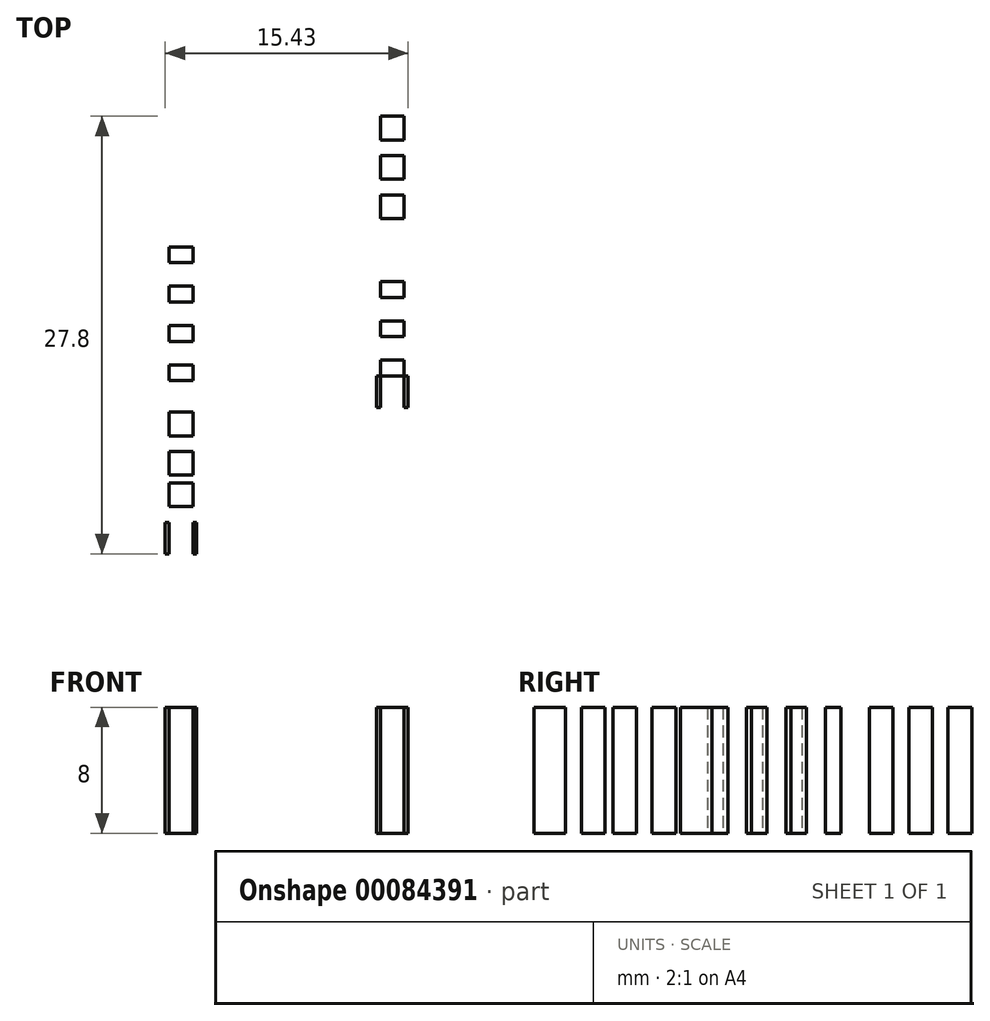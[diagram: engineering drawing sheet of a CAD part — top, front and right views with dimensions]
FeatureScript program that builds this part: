
annotation { "Feature Type Name" : "Feature", "Feature Type Description" : "" }
export const myFeature = defineFeature(function(context is Context, id is Id, definition is map)
    precondition{}
    {
        {
            var Q0;
            Q0=qCreatedBy(makeId("Top.planeOp"),FACE);
            var sketch = newSketch(context, id + "F0", { "sketchPlane" : qUnion([Q0])});
            skLineSegment(sketch, "E0.bottom", {"start": v(-61.05, 1.87) * mm, "end": v(-59.05, 1.87) * mm});
            skLineSegment(sketch, "E0.top", {"start": v(-61.05, -19.13) * mm, "end": v(-59.05, -19.13) * mm});
            skLineSegment(sketch, "E0.left", {"start": v(-61.05, 1.87) * mm, "end": v(-61.05, -19.13) * mm});
            skLineSegment(sketch, "E0.right", {"start": v(-59.05, 1.87) * mm, "end": v(-59.05, -19.13) * mm});
            skLineSegment(sketch, "E1", {"start": v(-61.05, -18.62) * mm, "end": v(-59.05, -18.62) * mm});
            skLineSegment(sketch, "E2", {"start": v(-61.05, -17.12) * mm, "end": v(-59.05, -17.12) * mm});
            skLineSegment(sketch, "E3", {"start": v(-60.8, 1.87) * mm, "end": v(-60.8, -19.13) * mm});
            skLineSegment(sketch, "E4", {"start": v(-60.8, -19.13) * mm, "end": v(-60.05, -19.13) * mm});
            skLineSegment(sketch, "E5", {"start": v(-59.3, 1.87) * mm, "end": v(-59.3, -19.13) * mm});
            skLineSegment(sketch, "E6.bottom", {"start": v(-60.8, 1.87) * mm, "end": v(-59.3, 1.87) * mm});
            skLineSegment(sketch, "E6.top", {"start": v(-60.8, 0.37) * mm, "end": v(-59.3, 0.37) * mm});
            skLineSegment(sketch, "E6.left", {"start": v(-60.8, 1.87) * mm, "end": v(-60.8, 0.37) * mm});
            skLineSegment(sketch, "E6.right", {"start": v(-59.3, 1.87) * mm, "end": v(-59.3, 0.37) * mm});
            skLineSegment(sketch, "E7.top", {"start": v(-60.8, -0.63) * mm, "end": v(-59.3, -0.63) * mm});
            skLineSegment(sketch, "E7.left", {"start": v(-60.8, 0.37) * mm, "end": v(-60.8, -0.63) * mm});
            skLineSegment(sketch, "E7.right", {"start": v(-59.3, 0.37) * mm, "end": v(-59.3, -0.63) * mm});
            skLineSegment(sketch, "E8.top", {"start": v(-60.8, -2.13) * mm, "end": v(-59.3, -2.13) * mm});
            skLineSegment(sketch, "E8.left", {"start": v(-60.8, -0.63) * mm, "end": v(-60.8, -2.13) * mm});
            skLineSegment(sketch, "E8.right", {"start": v(-59.3, -0.63) * mm, "end": v(-59.3, -2.13) * mm});
            skLineSegment(sketch, "E9.top", {"start": v(-60.8, -3.13) * mm, "end": v(-59.3, -3.13) * mm});
            skLineSegment(sketch, "E9.left", {"start": v(-60.8, -2.13) * mm, "end": v(-60.8, -3.13) * mm});
            skLineSegment(sketch, "E9.right", {"start": v(-59.3, -2.13) * mm, "end": v(-59.3, -3.13) * mm});
            skLineSegment(sketch, "E10.top", {"start": v(-60.8, -4.63) * mm, "end": v(-59.3, -4.63) * mm});
            skLineSegment(sketch, "E10.left", {"start": v(-60.8, -3.13) * mm, "end": v(-60.8, -4.63) * mm});
            skLineSegment(sketch, "E10.right", {"start": v(-59.3, -3.13) * mm, "end": v(-59.3, -4.63) * mm});
            skLineSegment(sketch, "E11.left", {"start": v(-60.8, -4.63) * mm, "end": v(-60.8, -5.63) * mm});
            skLineSegment(sketch, "E12.top", {"start": v(-60.8, -10.13) * mm, "end": v(-59.3, -10.13) * mm});
            skLineSegment(sketch, "E12.left", {"start": v(-60.8, -8.63) * mm, "end": v(-60.8, -10.13) * mm});
            skLineSegment(sketch, "E12.right", {"start": v(-59.3, -8.13) * mm, "end": v(-59.3, -10.13) * mm});
            skLineSegment(sketch, "E13.top", {"start": v(-60.8, -11.63) * mm, "end": v(-59.3, -11.63) * mm});
            skLineSegment(sketch, "E13.left", {"start": v(-60.8, -10.13) * mm, "end": v(-60.8, -11.63) * mm});
            skLineSegment(sketch, "E13.right", {"start": v(-59.3, -10.13) * mm, "end": v(-59.3, -11.63) * mm});
            skLineSegment(sketch, "E14.top", {"start": v(-60.8, -12.63) * mm, "end": v(-59.3, -12.63) * mm});
            skLineSegment(sketch, "E14.left", {"start": v(-60.8, -11.63) * mm, "end": v(-60.8, -12.63) * mm});
            skLineSegment(sketch, "E14.right", {"start": v(-59.3, -11.63) * mm, "end": v(-59.3, -12.63) * mm});
            skLineSegment(sketch, "E15.top", {"start": v(-60.8, -14.13) * mm, "end": v(-59.3, -14.13) * mm});
            skLineSegment(sketch, "E15.left", {"start": v(-60.8, -12.63) * mm, "end": v(-60.8, -14.13) * mm});
            skLineSegment(sketch, "E15.right", {"start": v(-59.3, -12.63) * mm, "end": v(-59.3, -14.13) * mm});
            skLineSegment(sketch, "E16.right", {"start": v(-59.3, -4.63) * mm, "end": v(-59.3, -5.63) * mm});
            skLineSegment(sketch, "E17", {"start": v(-60.8, -4.63) * mm, "end": v(-60.8, -6.63) * mm});
            skLineSegment(sketch, "E18", {"start": v(-59.3, -6.63) * mm, "end": v(-59.3, -4.63) * mm});
            skLineSegment(sketch, "E19", {"start": v(-59.3, -5.63) * mm, "end": v(-59.3, -4.63) * mm});
            skLineSegment(sketch, "E20", {"start": v(-60.8, -5.63) * mm, "end": v(-59.3, -5.63) * mm});
            skLineSegment(sketch, "E21", {"start": v(-60.8, -5.63) * mm, "end": v(-60.8, -7.13) * mm});
            skLineSegment(sketch, "E22", {"start": v(-59.3, -6.63) * mm, "end": v(-59.3, -5.63) * mm});
            skLineSegment(sketch, "E23", {"start": v(-60.8, -7.13) * mm, "end": v(-59.3, -7.13) * mm});
            skLineSegment(sketch, "E24.trimOffspring", {"start": v(-60.8, -6.63) * mm, "end": v(-60.8, -8.63) * mm});
            skLineSegment(sketch, "E25.trimOffspring", {"start": v(-59.3, -6.63) * mm, "end": v(-59.3, -8.63) * mm});
            skLineSegment(sketch, "E26.left", {"start": v(-60.8, -7.13) * mm, "end": v(-60.8, -8.63) * mm});
            skLineSegment(sketch, "E26.right", {"start": v(-59.3, -7.13) * mm, "end": v(-59.3, -8.63) * mm});
            skLineSegment(sketch, "E27.top", {"start": v(-60.8, -14.63) * mm, "end": v(-59.3, -14.63) * mm});
            skLineSegment(sketch, "E27.left", {"start": v(-60.8, -14.13) * mm, "end": v(-60.8, -14.63) * mm});
            skLineSegment(sketch, "E27.right", {"start": v(-59.3, -14.13) * mm, "end": v(-59.3, -14.63) * mm});
            skLineSegment(sketch, "E28.top", {"start": v(-60.8, -16.12) * mm, "end": v(-59.3, -16.12) * mm});
            skLineSegment(sketch, "E28.left", {"start": v(-60.8, -14.63) * mm, "end": v(-60.8, -16.12) * mm});
            skLineSegment(sketch, "E28.right", {"start": v(-59.3, -14.63) * mm, "end": v(-59.3, -16.12) * mm});
            skLineSegment(sketch, "E29.top", {"start": v(-60.8, -17.12) * mm, "end": v(-59.3, -17.12) * mm});
            skLineSegment(sketch, "E29.left", {"start": v(-60.8, -16.12) * mm, "end": v(-60.8, -17.12) * mm});
            skLineSegment(sketch, "E29.right", {"start": v(-59.3, -16.12) * mm, "end": v(-59.3, -17.12) * mm});
            skLineSegment(sketch, "E30.bottom", {"start": v(-47.62, 11.17) * mm, "end": v(-45.62, 11.17) * mm});
            skLineSegment(sketch, "E30.top", {"start": v(-47.62, -9.83) * mm, "end": v(-45.62, -9.83) * mm});
            skLineSegment(sketch, "E30.left", {"start": v(-47.62, 11.17) * mm, "end": v(-47.62, -9.83) * mm});
            skLineSegment(sketch, "E30.right", {"start": v(-45.62, 11.17) * mm, "end": v(-45.62, -9.83) * mm});
            skLineSegment(sketch, "E31", {"start": v(-47.62, -9.32) * mm, "end": v(-45.62, -9.32) * mm});
            skLineSegment(sketch, "E32", {"start": v(-47.62, -7.82) * mm, "end": v(-45.62, -7.82) * mm});
            skLineSegment(sketch, "E33", {"start": v(-47.37, 11.17) * mm, "end": v(-47.37, -9.83) * mm});
            skLineSegment(sketch, "E34", {"start": v(-47.37, -9.83) * mm, "end": v(-46.62, -9.83) * mm});
            skLineSegment(sketch, "E35", {"start": v(-45.87, 11.17) * mm, "end": v(-45.87, -9.83) * mm});
            skLineSegment(sketch, "E36.bottom", {"start": v(-47.37, 11.17) * mm, "end": v(-45.87, 11.17) * mm});
            skLineSegment(sketch, "E36.top", {"start": v(-47.37, 9.67) * mm, "end": v(-45.87, 9.67) * mm});
            skLineSegment(sketch, "E36.left", {"start": v(-47.37, 11.17) * mm, "end": v(-47.37, 9.67) * mm});
            skLineSegment(sketch, "E36.right", {"start": v(-45.87, 11.17) * mm, "end": v(-45.87, 9.67) * mm});
            skLineSegment(sketch, "E37.top", {"start": v(-47.37, 8.67) * mm, "end": v(-45.87, 8.67) * mm});
            skLineSegment(sketch, "E37.left", {"start": v(-47.37, 9.67) * mm, "end": v(-47.37, 8.67) * mm});
            skLineSegment(sketch, "E37.right", {"start": v(-45.87, 9.67) * mm, "end": v(-45.87, 8.67) * mm});
            skLineSegment(sketch, "E38.top", {"start": v(-47.37, 7.17) * mm, "end": v(-45.87, 7.17) * mm});
            skLineSegment(sketch, "E38.left", {"start": v(-47.37, 8.67) * mm, "end": v(-47.37, 7.17) * mm});
            skLineSegment(sketch, "E38.right", {"start": v(-45.87, 8.67) * mm, "end": v(-45.87, 7.17) * mm});
            skLineSegment(sketch, "E39.top", {"start": v(-47.37, 6.17) * mm, "end": v(-45.87, 6.17) * mm});
            skLineSegment(sketch, "E39.left", {"start": v(-47.37, 7.17) * mm, "end": v(-47.37, 6.17) * mm});
            skLineSegment(sketch, "E39.right", {"start": v(-45.87, 7.17) * mm, "end": v(-45.87, 6.17) * mm});
            skLineSegment(sketch, "E40.top", {"start": v(-47.37, 4.67) * mm, "end": v(-45.87, 4.67) * mm});
            skLineSegment(sketch, "E40.left", {"start": v(-47.37, 6.17) * mm, "end": v(-47.37, 4.67) * mm});
            skLineSegment(sketch, "E40.right", {"start": v(-45.87, 6.17) * mm, "end": v(-45.87, 4.67) * mm});
            skLineSegment(sketch, "E41.top", {"start": v(-47.37, 0.67) * mm, "end": v(-45.87, 0.67) * mm});
            skLineSegment(sketch, "E41.left", {"start": v(-47.37, 4.67) * mm, "end": v(-47.37, 3.67) * mm});
            skLineSegment(sketch, "E42.top", {"start": v(-47.37, -0.33) * mm, "end": v(-45.87, -0.33) * mm});
            skLineSegment(sketch, "E42.left", {"start": v(-47.37, 0.67) * mm, "end": v(-47.37, -0.33) * mm});
            skLineSegment(sketch, "E42.right", {"start": v(-45.87, 0.67) * mm, "end": v(-45.87, -0.33) * mm});
            skLineSegment(sketch, "E43.top", {"start": v(-47.37, -1.83) * mm, "end": v(-45.87, -1.83) * mm});
            skLineSegment(sketch, "E43.left", {"start": v(-47.37, -0.33) * mm, "end": v(-47.37, -1.83) * mm});
            skLineSegment(sketch, "E43.right", {"start": v(-45.87, -0.33) * mm, "end": v(-45.87, -1.83) * mm});
            skLineSegment(sketch, "E44.top", {"start": v(-47.37, -2.83) * mm, "end": v(-45.87, -2.83) * mm});
            skLineSegment(sketch, "E44.left", {"start": v(-47.37, -1.83) * mm, "end": v(-47.37, -2.83) * mm});
            skLineSegment(sketch, "E44.right", {"start": v(-45.87, -1.83) * mm, "end": v(-45.87, -2.83) * mm});
            skLineSegment(sketch, "E45.top", {"start": v(-47.37, -4.33) * mm, "end": v(-45.87, -4.33) * mm});
            skLineSegment(sketch, "E45.left", {"start": v(-47.37, -2.83) * mm, "end": v(-47.37, -4.33) * mm});
            skLineSegment(sketch, "E45.right", {"start": v(-45.87, -2.83) * mm, "end": v(-45.87, -4.33) * mm});
            skLineSegment(sketch, "E46.right", {"start": v(-45.87, 4.67) * mm, "end": v(-45.87, 3.67) * mm});
            skLineSegment(sketch, "E47", {"start": v(-47.37, 4.67) * mm, "end": v(-47.37, 2.67) * mm});
            skLineSegment(sketch, "E48", {"start": v(-45.87, 2.67) * mm, "end": v(-45.87, 4.67) * mm});
            skLineSegment(sketch, "E49", {"start": v(-45.87, 3.67) * mm, "end": v(-45.87, 4.67) * mm});
            skLineSegment(sketch, "E50", {"start": v(-47.37, 3.67) * mm, "end": v(-45.87, 3.67) * mm});
            skLineSegment(sketch, "E51", {"start": v(-47.37, 3.67) * mm, "end": v(-47.37, 2.17) * mm});
            skLineSegment(sketch, "E52", {"start": v(-45.87, 2.67) * mm, "end": v(-45.87, 3.67) * mm});
            skLineSegment(sketch, "E53", {"start": v(-47.37, 2.17) * mm, "end": v(-45.87, 2.17) * mm});
            skLineSegment(sketch, "E54.trimOffspring", {"start": v(-47.37, 2.67) * mm, "end": v(-47.37, 0.67) * mm});
            skLineSegment(sketch, "E55.trimOffspring", {"start": v(-45.87, 2.67) * mm, "end": v(-45.87, 0.67) * mm});
            skLineSegment(sketch, "E56.left", {"start": v(-47.37, 2.17) * mm, "end": v(-47.37, 0.67) * mm});
            skLineSegment(sketch, "E56.right", {"start": v(-45.87, 2.17) * mm, "end": v(-45.87, 0.67) * mm});
            skLineSegment(sketch, "E57.top", {"start": v(-47.37, -5.33) * mm, "end": v(-45.87, -5.33) * mm});
            skLineSegment(sketch, "E57.left", {"start": v(-47.37, -4.33) * mm, "end": v(-47.37, -5.33) * mm});
            skLineSegment(sketch, "E57.right", {"start": v(-45.87, -4.33) * mm, "end": v(-45.87, -5.33) * mm});
            skLineSegment(sketch, "E58.top", {"start": v(-47.37, -6.82) * mm, "end": v(-45.87, -6.82) * mm});
            skLineSegment(sketch, "E58.left", {"start": v(-47.37, -5.33) * mm, "end": v(-47.37, -6.82) * mm});
            skLineSegment(sketch, "E58.right", {"start": v(-45.87, -5.33) * mm, "end": v(-45.87, -6.82) * mm});
            skLineSegment(sketch, "E59.top", {"start": v(-47.37, -7.82) * mm, "end": v(-45.87, -7.82) * mm});
            skLineSegment(sketch, "E59.left", {"start": v(-47.37, -6.82) * mm, "end": v(-47.37, -7.82) * mm});
            skLineSegment(sketch, "E59.right", {"start": v(-45.87, -6.82) * mm, "end": v(-45.87, -7.82) * mm});
            skLineSegment(sketch, "E60", {"start": v(-59.3, -8.13) * mm, "end": v(-60.8, -8.13) * mm});
            skSolve(sketch);
        }
        {
            var Q0;
            {var subQ0=sQuery(id+"F0.wireOp",EDGE,"E0.left");var subQ1=sQuery(id+"F0.wireOp",EDGE,"E0.top");var subQ2=makeQuery(id+"F0.imprint","INTERSECT",VERTEX,{"derivedFrom":[subQ1,subQ0]});Q0=makeQuery(id+"F0.imprint","IMPRINT",FACE,{"disambiguationData":[TD([[makeQuery(id+"F0.imprint","IMPRINT",EDGE,{"disambiguationData":[TD([[subQ2,1.0]])],"derivedFrom":subQ0}),1.0]])]});}
            var Q1;
            {var subQ0=sQuery(id+"F0.wireOp",EDGE,"E0.right");var subQ1=sQuery(id+"F0.wireOp",EDGE,"E0.top");var subQ2=makeQuery(id+"F0.imprint","INTERSECT",VERTEX,{"derivedFrom":[subQ1,subQ0]});Q1=makeQuery(id+"F0.imprint","IMPRINT",FACE,{"disambiguationData":[TD([[makeQuery(id+"F0.imprint","IMPRINT",EDGE,{"disambiguationData":[TD([[subQ2,1.0]])],"derivedFrom":subQ1}),1.0]])]});}
            var Q2;
            {var subQ0=sQuery(id+"F0.wireOp",EDGE,"E30.left");var subQ1=sQuery(id+"F0.wireOp",EDGE,"E30.top");var subQ2=makeQuery(id+"F0.imprint","INTERSECT",VERTEX,{"derivedFrom":[subQ1,subQ0]});Q2=makeQuery(id+"F0.imprint","IMPRINT",FACE,{"disambiguationData":[TD([[makeQuery(id+"F0.imprint","IMPRINT",EDGE,{"disambiguationData":[TD([[subQ2,1.0]])],"derivedFrom":subQ0}),1.0]])]});}
            var Q3;
            {var subQ0=sQuery(id+"F0.wireOp",EDGE,"E30.right");var subQ1=sQuery(id+"F0.wireOp",EDGE,"E30.top");var subQ2=makeQuery(id+"F0.imprint","INTERSECT",VERTEX,{"derivedFrom":[subQ1,subQ0]});Q3=makeQuery(id+"F0.imprint","IMPRINT",FACE,{"disambiguationData":[TD([[makeQuery(id+"F0.imprint","IMPRINT",EDGE,{"disambiguationData":[TD([[subQ2,1.0]])],"derivedFrom":subQ1}),1.0]])]});}
            var Q4;
            {var subQ5=sQuery(id+"F0.wireOp",EDGE,"E4");Q4=makeQuery(id+"F0.imprint","IMPRINT",FACE,{"disambiguationData":[TD([[makeQuery(id+"F0.imprint","IMPRINT",EDGE,{"derivedFrom":subQ5}),1.0]])]});}
            var Q5;
            {var subQ0=sQuery(id+"F0.wireOp",EDGE,"E1");var subQ1=sQuery(id+"F0.wireOp",EDGE,"E0.left");var subQ2=makeQuery(id+"F0.imprint","INTERSECT",VERTEX,{"derivedFrom":[subQ1,subQ0]});Q5=makeQuery(id+"F0.imprint","IMPRINT",FACE,{"disambiguationData":[TD([[makeQuery(id+"F0.imprint","IMPRINT",EDGE,{"disambiguationData":[TD([[subQ2,1.0]])],"derivedFrom":subQ1}),1.0]])]});}
            var Q6;
            {var subQ0=sQuery(id+"F0.wireOp",EDGE,"E1");var subQ1=sQuery(id+"F0.wireOp",EDGE,"E0.right");var subQ2=makeQuery(id+"F0.imprint","INTERSECT",VERTEX,{"derivedFrom":[subQ1,subQ0]});Q6=makeQuery(id+"F0.imprint","IMPRINT",FACE,{"disambiguationData":[TD([[makeQuery(id+"F0.imprint","IMPRINT",EDGE,{"disambiguationData":[TD([[subQ2,1.0]])],"derivedFrom":subQ1}),-1.0]])]});}
            var Q7;
            {var subQ0=sQuery(id+"F0.wireOp",EDGE,"E31");var subQ1=sQuery(id+"F0.wireOp",EDGE,"E30.left");var subQ2=makeQuery(id+"F0.imprint","INTERSECT",VERTEX,{"derivedFrom":[subQ1,subQ0]});Q7=makeQuery(id+"F0.imprint","IMPRINT",FACE,{"disambiguationData":[TD([[makeQuery(id+"F0.imprint","IMPRINT",EDGE,{"disambiguationData":[TD([[subQ2,1.0]])],"derivedFrom":subQ1}),1.0]])]});}
            var Q8;
            {var subQ0=sQuery(id+"F0.wireOp",EDGE,"E31");var subQ1=sQuery(id+"F0.wireOp",EDGE,"E30.right");var subQ2=makeQuery(id+"F0.imprint","INTERSECT",VERTEX,{"derivedFrom":[subQ1,subQ0]});Q8=makeQuery(id+"F0.imprint","IMPRINT",FACE,{"disambiguationData":[TD([[makeQuery(id+"F0.imprint","IMPRINT",EDGE,{"disambiguationData":[TD([[subQ2,1.0]])],"derivedFrom":subQ1}),-1.0]])]});}
            var Q9;
            {var subQ3=sQuery(id+"F0.wireOp",EDGE,"E6.left");Q9=makeQuery(id+"F0.imprint","IMPRINT",FACE,{"disambiguationData":[TD([[makeQuery(id+"F0.imprint","IMPRINT",EDGE,{"derivedFrom":subQ3}),-1.0]])]});}
            var Q10;
            {var subQ0=sQuery(id+"F0.wireOp",EDGE,"E6.right");Q10=makeQuery(id+"F0.imprint","IMPRINT",FACE,{"disambiguationData":[TD([[makeQuery(id+"F0.imprint","IMPRINT",EDGE,{"derivedFrom":subQ0}),1.0]])]});}
            var Q11;
            {var subQ3=sQuery(id+"F0.wireOp",EDGE,"E36.left");Q11=makeQuery(id+"F0.imprint","IMPRINT",FACE,{"disambiguationData":[TD([[makeQuery(id+"F0.imprint","IMPRINT",EDGE,{"derivedFrom":subQ3}),-1.0]])]});}
            var Q12;
            {var subQ3=sQuery(id+"F0.wireOp",EDGE,"E36.right");Q12=makeQuery(id+"F0.imprint","IMPRINT",FACE,{"disambiguationData":[TD([[makeQuery(id+"F0.imprint","IMPRINT",EDGE,{"derivedFrom":subQ3}),1.0]])]});}
            var Q13;
            {var subQ0=sQuery(id+"F0.wireOp",EDGE,"E34");Q13=makeQuery(id+"F0.imprint","IMPRINT",FACE,{"disambiguationData":[TD([[makeQuery(id+"F0.imprint","IMPRINT",EDGE,{"derivedFrom":subQ0}),1.0]])]});}
            var Q14;
            Q14=makeQuery(id+"F0.imprint","IMPRINT",FACE,{"disambiguationData":[TD([[makeQuery(id+"F0.imprint","IMPRINT",EDGE,{"derivedFrom":sQuery(id+"F0.wireOp",EDGE,"E6.bottom")}),-1.0]])]});
            var Q15;
            Q15=makeQuery(id+"F0.imprint","IMPRINT",FACE,{"disambiguationData":[TD([[makeQuery(id+"F0.imprint","IMPRINT",EDGE,{"derivedFrom":sQuery(id+"F0.wireOp",EDGE,"E10.top")}),-1.0]])]});
            var Q16;
            Q16=makeQuery(id+"F0.imprint","IMPRINT",FACE,{"disambiguationData":[TD([[makeQuery(id+"F0.imprint","IMPRINT",EDGE,{"derivedFrom":sQuery(id+"F0.wireOp",EDGE,"E8.top")}),-1.0]])]});
            var Q17;
            Q17=makeQuery(id+"F0.imprint","IMPRINT",FACE,{"disambiguationData":[TD([[makeQuery(id+"F0.imprint","IMPRINT",EDGE,{"derivedFrom":sQuery(id+"F0.wireOp",EDGE,"E6.top")}),-1.0]])]});
            var Q18;
            {var subQ0=sQuery(id+"F0.wireOp",EDGE,"E23");Q18=makeQuery(id+"F0.imprint","IMPRINT",FACE,{"disambiguationData":[TD([[makeQuery(id+"F0.imprint","IMPRINT",EDGE,{"derivedFrom":subQ0}),-1.0]])]});}
            var Q19;
            Q19=makeQuery(id+"F0.imprint","IMPRINT",FACE,{"disambiguationData":[TD([[makeQuery(id+"F0.imprint","IMPRINT",EDGE,{"derivedFrom":sQuery(id+"F0.wireOp",EDGE,"E12.top")}),-1.0]])]});
            var Q20;
            Q20=makeQuery(id+"F0.imprint","IMPRINT",FACE,{"disambiguationData":[TD([[makeQuery(id+"F0.imprint","IMPRINT",EDGE,{"derivedFrom":sQuery(id+"F0.wireOp",EDGE,"E14.top")}),-1.0]])]});
            var Q21;
            Q21=makeQuery(id+"F0.imprint","IMPRINT",FACE,{"disambiguationData":[TD([[makeQuery(id+"F0.imprint","IMPRINT",EDGE,{"derivedFrom":sQuery(id+"F0.wireOp",EDGE,"E27.top")}),-1.0]])]});
            var Q22;
            {var subQ5=sQuery(id+"F0.wireOp",EDGE,"E29.top");Q22=makeQuery(id+"F0.imprint","IMPRINT",FACE,{"disambiguationData":[TD([[makeQuery(id+"F0.imprint","IMPRINT",EDGE,{"derivedFrom":subQ5}),-1.0]])]});}
            var Q23;
            Q23=makeQuery(id+"F0.imprint","IMPRINT",FACE,{"disambiguationData":[TD([[makeQuery(id+"F0.imprint","IMPRINT",EDGE,{"derivedFrom":sQuery(id+"F0.wireOp",EDGE,"E37.top")}),-1.0]])]});
            var Q24;
            Q24=makeQuery(id+"F0.imprint","IMPRINT",FACE,{"disambiguationData":[TD([[makeQuery(id+"F0.imprint","IMPRINT",EDGE,{"derivedFrom":sQuery(id+"F0.wireOp",EDGE,"E39.top")}),-1.0]])]});
            var Q25;
            Q25=makeQuery(id+"F0.imprint","IMPRINT",FACE,{"disambiguationData":[TD([[makeQuery(id+"F0.imprint","IMPRINT",EDGE,{"derivedFrom":sQuery(id+"F0.wireOp",EDGE,"E50")}),-1.0]])]});
            var Q26;
            Q26=makeQuery(id+"F0.imprint","IMPRINT",FACE,{"disambiguationData":[TD([[makeQuery(id+"F0.imprint","IMPRINT",EDGE,{"derivedFrom":sQuery(id+"F0.wireOp",EDGE,"E42.left")}),1.0]])]});
            var Q27;
            Q27=makeQuery(id+"F0.imprint","IMPRINT",FACE,{"disambiguationData":[TD([[makeQuery(id+"F0.imprint","IMPRINT",EDGE,{"derivedFrom":sQuery(id+"F0.wireOp",EDGE,"E43.top")}),-1.0]])]});
            var Q28;
            Q28=makeQuery(id+"F0.imprint","IMPRINT",FACE,{"disambiguationData":[TD([[makeQuery(id+"F0.imprint","IMPRINT",EDGE,{"derivedFrom":sQuery(id+"F0.wireOp",EDGE,"E45.top")}),-1.0]])]});
            var Q29;
            Q29=makeQuery(id+"F0.imprint","IMPRINT",FACE,{"disambiguationData":[TD([[makeQuery(id+"F0.imprint","IMPRINT",EDGE,{"derivedFrom":sQuery(id+"F0.wireOp",EDGE,"E58.top")}),-1.0]])]});
            extrude(context, id + "F1", {"entities" : qUnion([Q0, Q1, Q2, Q3, Q4, Q5, Q6, Q7, Q8, Q9, Q10, Q11, Q12, Q13, Q14, Q15, Q16, Q17, Q18, Q19, Q20, Q21, Q22, Q23, Q24, Q25, Q26, Q27, Q28, Q29]), "depth" : 8 * mm});
        }
    });
